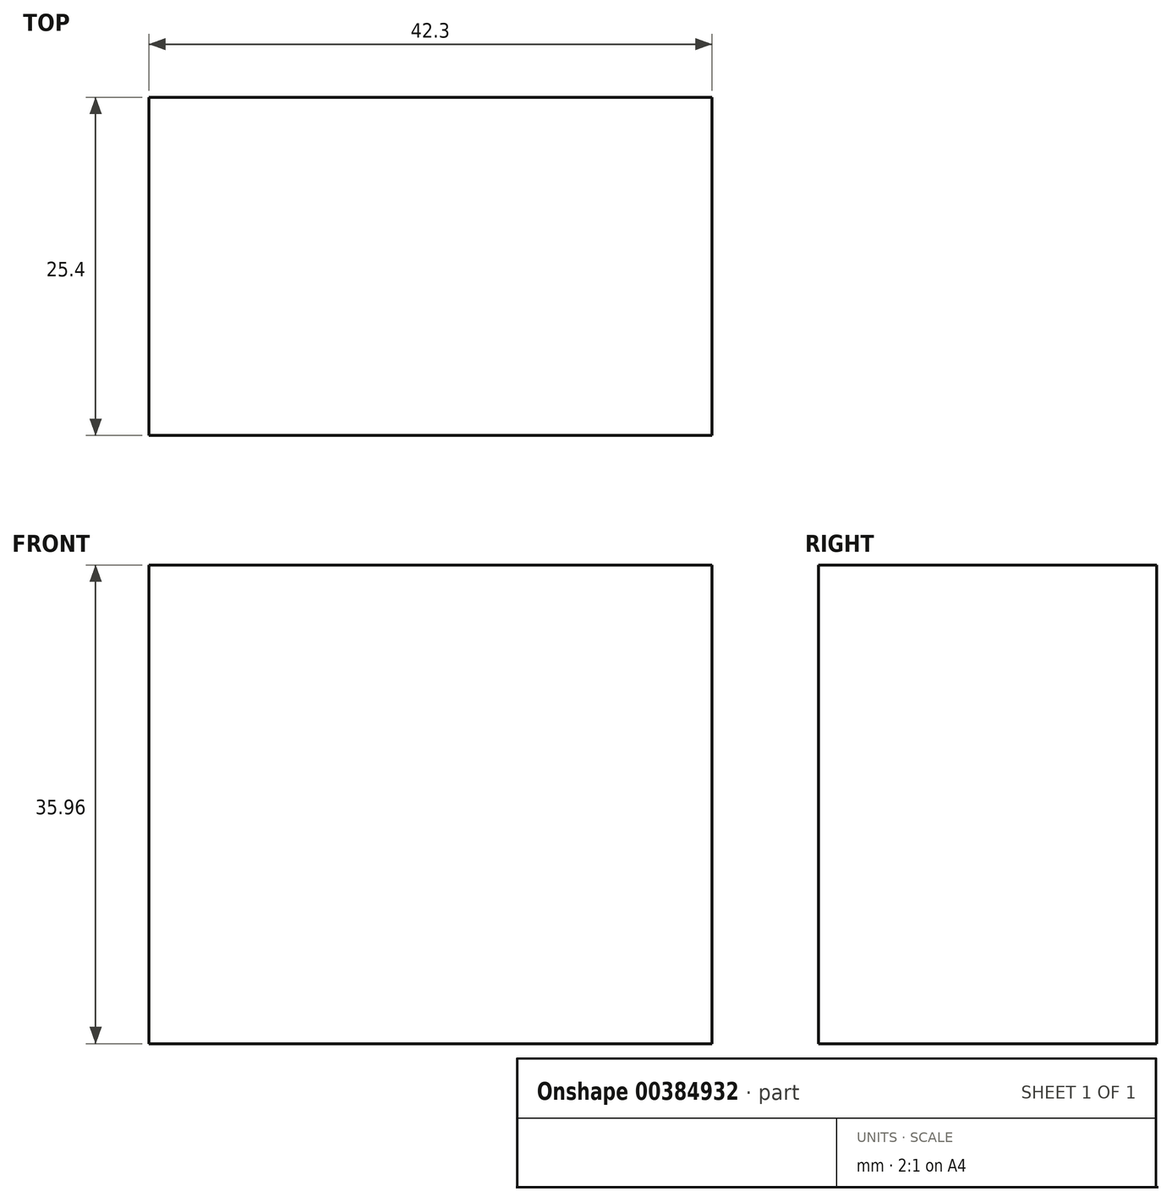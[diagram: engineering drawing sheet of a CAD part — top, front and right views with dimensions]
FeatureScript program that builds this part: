
annotation { "Feature Type Name" : "Feature", "Feature Type Description" : "" }
export const myFeature = defineFeature(function(context is Context, id is Id, definition is map)
    precondition{}
    {
        {
            var Q0;
            Q0=qCreatedBy(makeId("Front.planeOp"),FACE);
            var sketch = newSketch(context, id + "F0", { "sketchPlane" : qUnion([Q0])});
            skLineSegment(sketch, "E0.bottom", {"start": v(-93.71, 66.14) * mm, "end": v(-51.4, 66.14) * mm});
            skLineSegment(sketch, "E0.top", {"start": v(-93.71, 30.18) * mm, "end": v(-51.4, 30.18) * mm});
            skLineSegment(sketch, "E0.left", {"start": v(-93.71, 66.14) * mm, "end": v(-93.71, 30.18) * mm});
            skLineSegment(sketch, "E0.right", {"start": v(-51.4, 66.14) * mm, "end": v(-51.4, 30.18) * mm});
            skSolve(sketch);
        }
        {
            var Q0;
            Q0=makeQuery(id+"F0.imprint","IMPRINT",FACE,{"disambiguationData":[TD([[makeQuery(id+"F0.imprint","IMPRINT",EDGE,{"derivedFrom":sQuery(id+"F0.wireOp",EDGE,"E0.bottom")}),-1.0]])]});
            extrude(context, id + "F1", {"entities" : qUnion([Q0]), "depth" : 25.4 * mm});
        }
    });
